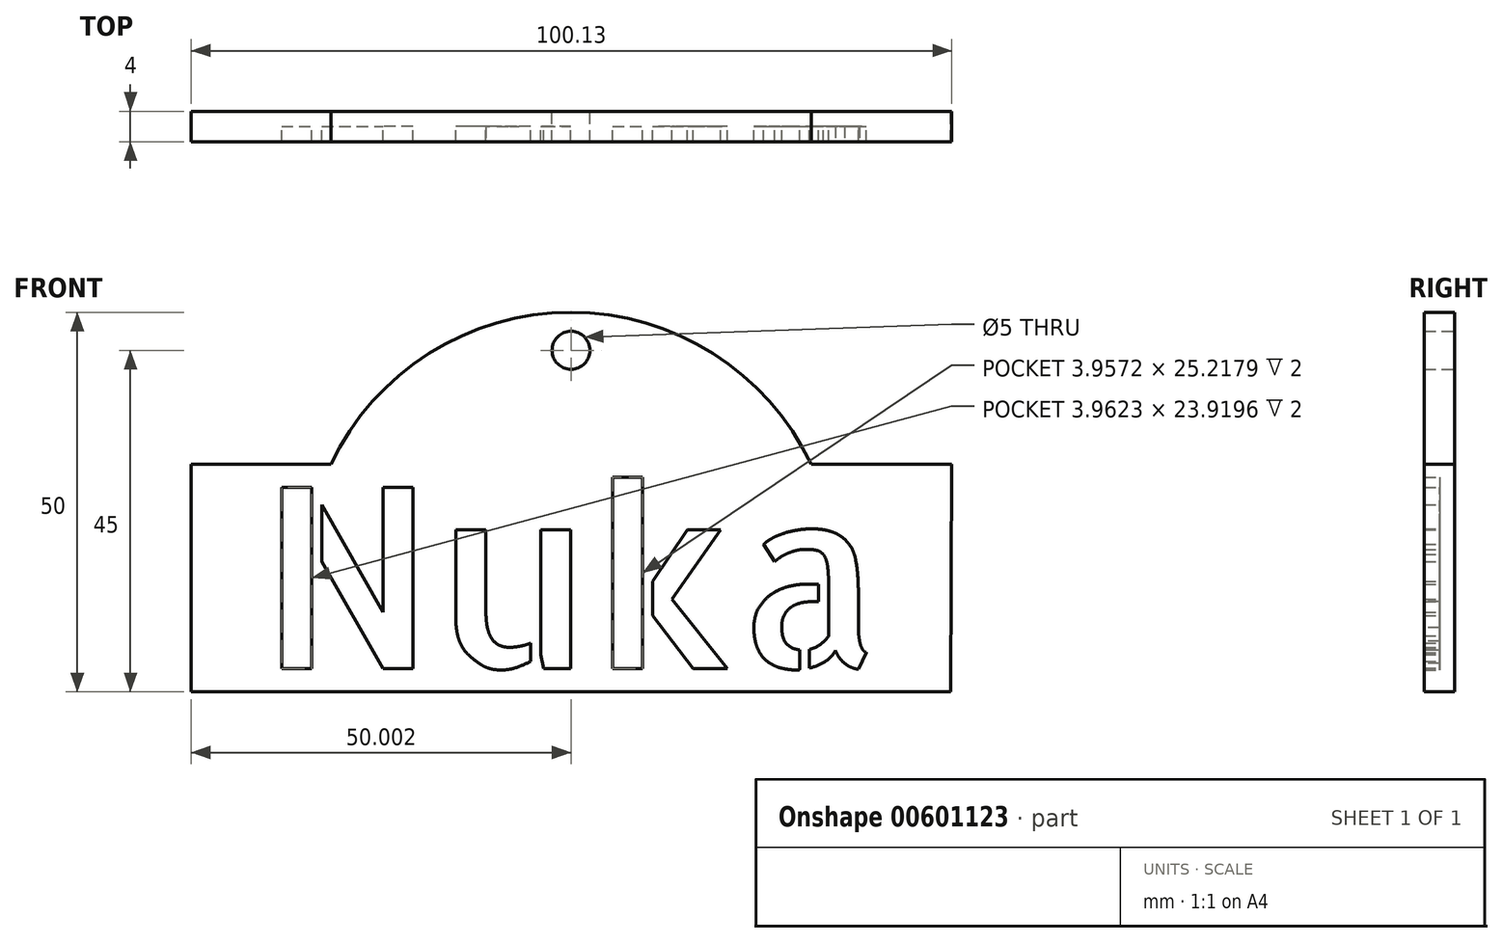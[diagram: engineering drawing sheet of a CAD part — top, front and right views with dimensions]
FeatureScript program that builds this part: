
annotation { "Feature Type Name" : "Feature", "Feature Type Description" : "" }
export const myFeature = defineFeature(function(context is Context, id is Id, definition is map)
    precondition{}
    {
        {
            var Q0;
            Q0=qCreatedBy(makeId("Front.planeOp"),FACE);
            var sketch = newSketch(context, id + "F0", { "sketchPlane" : qUnion([Q0])});
            skLineSegment(sketch, "E0.bottom", {"start": v(-197.54, 2.03) * mm, "end": v(-179.16, 2.03) * mm});
            skLineSegment(sketch, "E0.top", {"start": v(-197.54, -27.97) * mm, "end": v(-97.54, -27.97) * mm});
            skLineSegment(sketch, "E0.right", {"start": v(-97.4, 2.03) * mm, "end": v(-97.54, -27.97) * mm});
            skArc(sketch, "E1", {"start": v(-115.92, 2.03) * mm, "mid": v(-147.54, 22.03) * mm, "end": v(-179.16, 2.03) * mm});
            skCircle(sketch, "E2", {"center": v(-147.54, 17.03) * mm, "radius": 2.5 * mm});
            skLineSegment(sketch, "E3", {"start": v(-197.54, 2.03) * mm, "end": v(-197.54, -27.97) * mm});
            skPoint(sketch, "E4", {"position": v(-197.54, -12.97) * mm});
            skPoint(sketch, "E5", {"position": v(-147.54, -27.97) * mm});
            skText(sketch, "E6", { "text": "Nuka", "fontName": "AllertaStencil-Regular.ttf"});
            skPoint(sketch, "E7", {"position": v(-106.44, -12.97) * mm});
            skPoint(sketch, "E8", {"position": v(-147.54, -24.93) * mm});
            skLineSegment(sketch, "E9.trimOffspring", {"start": v(-115.92, 2.03) * mm, "end": v(-97.4, 2.03) * mm});
            const initialGuessF0  = {"E6": [-0.18863, -0.02493, 1, 0, 0.02393]};
            skSetInitialGuess(sketch, initialGuessF0);
            skSolve(sketch);
        }
        {
            var Q0;
            Q0=makeQuery(id+"F0.imprint","IMPRINT",FACE,{"disambiguationData":[TD([[makeQuery(id+"F0.imprint","IMPRINT",EDGE,{"derivedFrom":sQuery(id+"F0.wireOp",EDGE,"E0.bottom")}),-1.0]])]});
            var Q1;
            Q1 = qSketchRegion(id + "F0", true);
            var Q2;
            Q2=makeQuery(id+"F0.imprint","IMPRINT",FACE,{"disambiguationData":[TD([[makeQuery(id+"F0.imprint","IMPRINT",EDGE,{"derivedFrom":sQuery(id+"F0.wireOp",EDGE,"E6.sketch_text.stroke-11")}),-1.0]])]});
            var Q3;
            Q3=makeQuery(id+"F0.imprint","IMPRINT",FACE,{"disambiguationData":[TD([[makeQuery(id+"F0.imprint","IMPRINT",EDGE,{"derivedFrom":sQuery(id+"F0.wireOp",EDGE,"E6.sketch_text.stroke-47")}),-1.0]])]});
            var Q4;
            Q4=makeQuery(id+"F0.imprint","IMPRINT",FACE,{"disambiguationData":[TD([[makeQuery(id+"F0.imprint","IMPRINT",EDGE,{"derivedFrom":sQuery(id+"F0.wireOp",EDGE,"E6.sketch_text.stroke-66")}),-1.0]])]});
            var Q5;
            Q5=makeQuery(id+"F0.imprint","IMPRINT",FACE,{"disambiguationData":[TD([[makeQuery(id+"F0.imprint","IMPRINT",EDGE,{"derivedFrom":sQuery(id+"F0.wireOp",EDGE,"E6.sketch_text.stroke-0")}),-1.0]])]});
            var Q6;
            Q6=makeQuery(id+"F0.imprint","IMPRINT",FACE,{"disambiguationData":[TD([[makeQuery(id+"F0.imprint","IMPRINT",EDGE,{"derivedFrom":sQuery(id+"F0.wireOp",EDGE,"E6.sketch_text.stroke-7")}),-1.0]])]});
            var Q7;
            Q7=makeQuery(id+"F0.imprint","IMPRINT",FACE,{"disambiguationData":[TD([[makeQuery(id+"F0.imprint","IMPRINT",EDGE,{"derivedFrom":sQuery(id+"F0.wireOp",EDGE,"E6.sketch_text.stroke-43")}),-1.0]])]});
            var Q8;
            Q8=makeQuery(id+"F0.imprint","IMPRINT",FACE,{"disambiguationData":[TD([[makeQuery(id+"F0.imprint","IMPRINT",EDGE,{"derivedFrom":sQuery(id+"F0.wireOp",EDGE,"E6.sketch_text.stroke-31")}),-1.0]])]});
            var Q9;
            Q9=makeQuery(id+"F0.imprint","IMPRINT",FACE,{"disambiguationData":[TD([[makeQuery(id+"F0.imprint","IMPRINT",EDGE,{"derivedFrom":sQuery(id+"F0.wireOp",EDGE,"E6.sketch_text.stroke-36")}),-1.0]])]});
            extrude(context, id + "F1", {"entities" : qUnion([Q0, Q1, Q2, Q3, Q4, Q5, Q6, Q7, Q8, Q9]), "depth" : 2 * mm, "offsetDistance" : 25 * mm});
        }
        {
            var Q0;
            Q0=makeQuery(id+"F0.imprint","IMPRINT",FACE,{"disambiguationData":[TD([[makeQuery(id+"F0.imprint","IMPRINT",EDGE,{"derivedFrom":sQuery(id+"F0.wireOp",EDGE,"E0.bottom")}),-1.0]])]});
            extrude(context, id + "F2", {"entities" : qUnion([Q0]), "operationType" : NewBodyOperationType.ADD, "depth" : 4 * mm, "offsetDistance" : 25 * mm});
        }
    });
